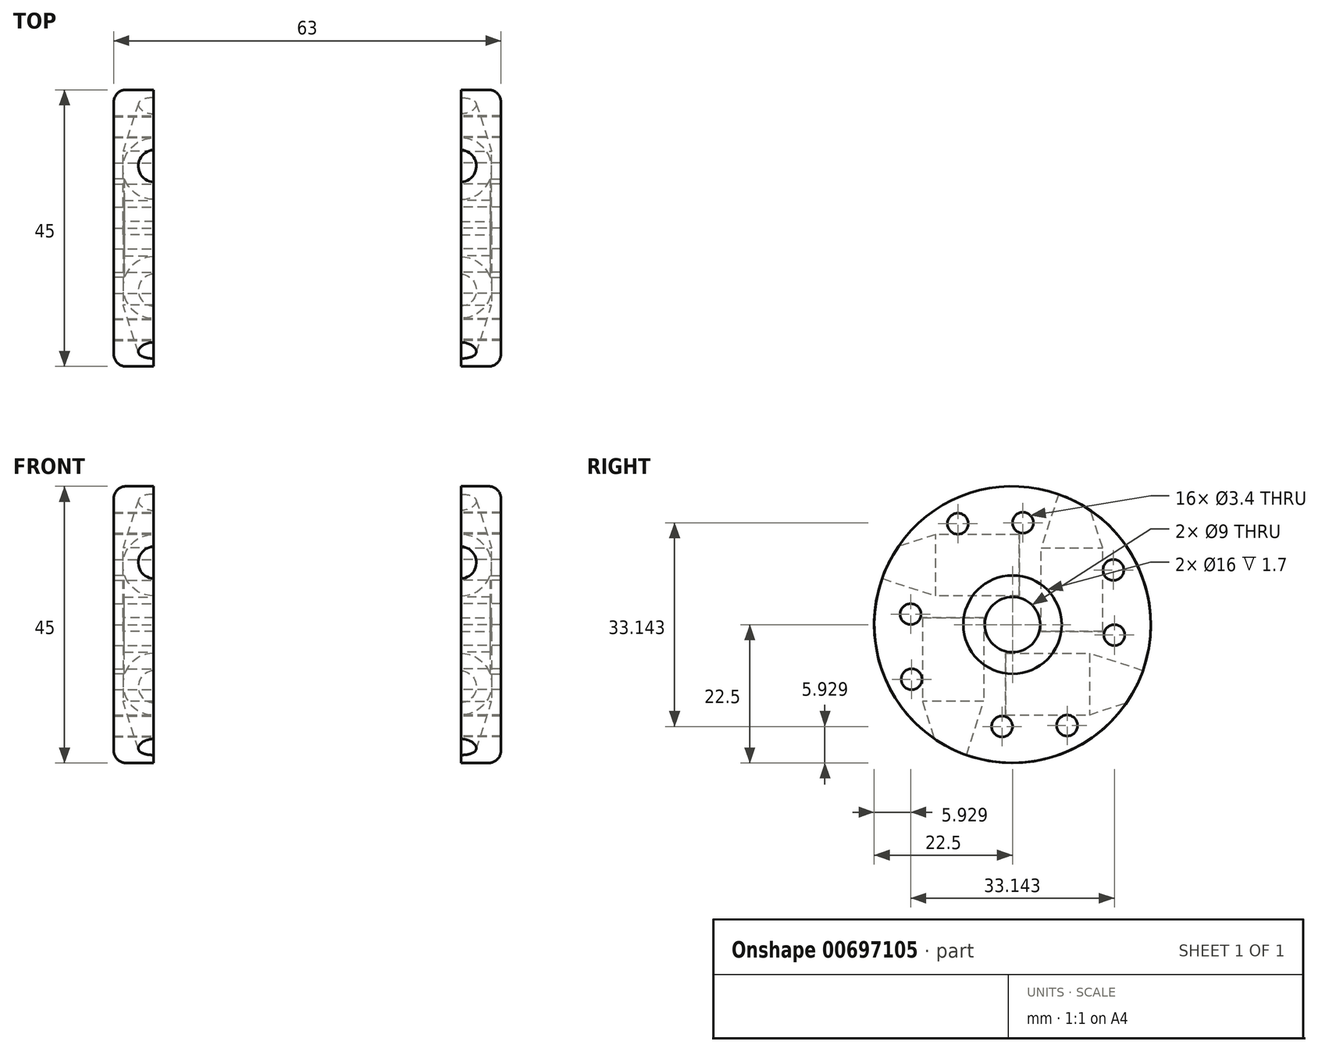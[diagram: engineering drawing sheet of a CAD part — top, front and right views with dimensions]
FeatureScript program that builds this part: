
annotation { "Feature Type Name" : "Feature", "Feature Type Description" : "" }
export const myFeature = defineFeature(function(context is Context, id is Id, definition is map)
    precondition{}
    {
        {
            var Q0;
            Q0=qCreatedBy(makeId("Right.planeOp"),FACE);
            var sketch = newSketch(context, id + "F0", { "sketchPlane" : qUnion([Q0])});
            skCircle(sketch, "E0", {"center": v(0, 0) * mm, "radius": 22.5 * mm});
            skCircle(sketch, "E1", {"center": v(0, 0) * mm, "radius": 4.5 * mm});
            skCircle(sketch, "E2", {"center": v(1.7, 16.57) * mm, "radius": 1.7 * mm});
            skCircle(sketch, "E3", {"center": v(-8.89, 16.41) * mm, "radius": 1.7 * mm});
            skCircle(sketch, "E4.1.0", {"center": v(-16.57, 1.7) * mm, "radius": 1.7 * mm});
            skCircle(sketch, "E4.1.1", {"center": v(-16.41, -8.89) * mm, "radius": 1.7 * mm});
            skCircle(sketch, "E4.2.0", {"center": v(-1.7, -16.57) * mm, "radius": 1.7 * mm});
            skCircle(sketch, "E4.2.1", {"center": v(8.89, -16.41) * mm, "radius": 1.7 * mm});
            skCircle(sketch, "E4.3.0", {"center": v(16.57, -1.7) * mm, "radius": 1.7 * mm});
            skCircle(sketch, "E4.3.1", {"center": v(16.41, 8.89) * mm, "radius": 1.7 * mm});
            skSolve(sketch);
        }
        {
            var Q0;
            Q0=makeQuery(id+"F0.imprint","IMPRINT",FACE,{"disambiguationData":[TD([[makeQuery(id+"F0.imprint","IMPRINT",EDGE,{"derivedFrom":sQuery(id+"F0.wireOp",EDGE,"E0")}),1.0]])]});
            var Q1;
            Q1=makeQuery(id+"F0.imprint","IMPRINT",FACE,{"disambiguationData":[TD([[makeQuery(id+"F0.imprint","IMPRINT",EDGE,{"derivedFrom":sQuery(id+"F0.wireOp",EDGE,"E1")}),-1.0]])]});
            extrude(context, id + "F1", {"entities" : qUnion([Q0, Q1]), "depth" : 6.5 * mm, "offsetDistance" : 25 * mm});
        }
        {
            var Q0;
            Q0=qCreatedBy(makeId("Top.planeOp"),FACE);
            var sketch = newSketch(context, id + "F2", { "sketchPlane" : qUnion([Q0])});
            skLineSegment(sketch, "E5", {"start": v(-19.71, 0) * mm, "end": v(30.41, 0) * mm});
            skSolve(sketch);
        }
        {
            var Q0;
            Q0=qCreatedBy(makeId("Right.planeOp"),FACE);
            var sketch = newSketch(context, id + "F3", { "sketchPlane" : qUnion([Q0])});
            skLineSegment(sketch, "E6.top", {"start": v(1.1, 9.67) * mm, "end": v(1.1, 4.67) * mm});
            skLineSegment(sketch, "E6.left", {"start": v(-12.5, 9.67) * mm, "end": v(1.1, 9.67) * mm});
            skLineSegment(sketch, "E6.right", {"start": v(-12.5, 4.67) * mm, "end": v(1.1, 4.67) * mm});
            skLineSegment(sketch, "E7", {"start": v(-12.5, 4.67) * mm, "end": v(-24.5, 8.57) * mm});
            skLineSegment(sketch, "E8", {"start": v(-24.5, 8.57) * mm, "end": v(-24.5, 9.67) * mm});
            skLineSegment(sketch, "E9", {"start": v(-24.5, 9.67) * mm, "end": v(-12.5, 9.67) * mm});
            skSolve(sketch);
        }
        {
            var Q0;
            Q0=makeQuery(id+"F3.imprint","IMPRINT",FACE,{"disambiguationData":[TD([[makeQuery(id+"F3.imprint","IMPRINT",EDGE,{"derivedFrom":sQuery(id+"F3.wireOp",EDGE,"E6.top")}),-1.0]])]});
            var Q1;
            Q1=sQuery(id+"F3.wireOp",EDGE,"E9");
            revolve(context, id + "F4", {"entities" : qUnion([Q0]), "axis" : qUnion([Q1]), "revolveType" : RevolveType.FULL});
        }
        {
            var Q0;
            Q0=makeQuery(id+"F4.opRevolve","SWEPT_BODY",BODY,{"disambiguationData":[OSD([sQuery(id+"F3.wireOp",EDGE,"E6.top"),sQuery(id+"F3.wireOp",EDGE,"E6.left"),sQuery(id+"F3.wireOp",EDGE,"E6.right"),sQuery(id+"F3.wireOp",EDGE,"E7"),sQuery(id+"F3.wireOp",EDGE,"E8"),sQuery(id+"F3.wireOp",EDGE,"E9")])]});
            var Q1;
            Q1=sQuery(id+"F2.wireOp",EDGE,"E5");
            circularPattern(context, id + "F5", {"entities" : qUnion([Q0]), "axis" : qUnion([Q1]), "angle" : 360 * degree, "instanceCount" : 4, "equalSpace" : true});
        }
        {
            var Q0;
            Q0=makeQuery(id+"F4.opRevolve","SWEPT_BODY",BODY,{"disambiguationData":[OSD([sQuery(id+"F3.wireOp",EDGE,"E6.top"),sQuery(id+"F3.wireOp",EDGE,"E6.left"),sQuery(id+"F3.wireOp",EDGE,"E6.right"),sQuery(id+"F3.wireOp",EDGE,"E7"),sQuery(id+"F3.wireOp",EDGE,"E8"),sQuery(id+"F3.wireOp",EDGE,"E9")])]});
            var Q1;
            Q1=makeQuery(id+"F5.opPattern","COPY",BODY,{"derivedFrom":makeQuery(id+"F4.opRevolve","SWEPT_BODY",BODY,{"disambiguationData":[OSD([sQuery(id+"F3.wireOp",EDGE,"E6.top"),sQuery(id+"F3.wireOp",EDGE,"E6.left"),sQuery(id+"F3.wireOp",EDGE,"E6.right"),sQuery(id+"F3.wireOp",EDGE,"E7"),sQuery(id+"F3.wireOp",EDGE,"E8"),sQuery(id+"F3.wireOp",EDGE,"E9")])]}),"instanceName":"3"});
            var Q2;
            Q2=makeQuery(id+"F5.opPattern","COPY",BODY,{"derivedFrom":makeQuery(id+"F4.opRevolve","SWEPT_BODY",BODY,{"disambiguationData":[OSD([sQuery(id+"F3.wireOp",EDGE,"E6.top"),sQuery(id+"F3.wireOp",EDGE,"E6.left"),sQuery(id+"F3.wireOp",EDGE,"E6.right"),sQuery(id+"F3.wireOp",EDGE,"E7"),sQuery(id+"F3.wireOp",EDGE,"E8"),sQuery(id+"F3.wireOp",EDGE,"E9")])]}),"instanceName":"2"});
            var Q3;
            Q3=makeQuery(id+"F5.opPattern","COPY",BODY,{"derivedFrom":makeQuery(id+"F4.opRevolve","SWEPT_BODY",BODY,{"disambiguationData":[OSD([sQuery(id+"F3.wireOp",EDGE,"E6.top"),sQuery(id+"F3.wireOp",EDGE,"E6.left"),sQuery(id+"F3.wireOp",EDGE,"E6.right"),sQuery(id+"F3.wireOp",EDGE,"E7"),sQuery(id+"F3.wireOp",EDGE,"E8"),sQuery(id+"F3.wireOp",EDGE,"E9")])]}),"instanceName":"1"});
            var Q4;
            Q4=makeQuery(id+"F1.opExtrude","SWEPT_BODY",BODY,{"disambiguationData":[OSD([sQuery(id+"F0.wireOp",EDGE,"E0"),sQuery(id+"F0.wireOp",EDGE,"E1"),sQuery(id+"F0.wireOp",EDGE,"E2"),sQuery(id+"F0.wireOp",EDGE,"cbc2b849-6399-4062-8aac-5185108daa26.1.0"),sQuery(id+"F0.wireOp",EDGE,"cbc2b849-6399-4062-8aac-5185108daa26.2.0"),sQuery(id+"F0.wireOp",EDGE,"cbc2b849-6399-4062-8aac-5185108daa26.3.0")])]});
            booleanBodies(context, id + "F6", {"operationType" : BooleanOperationType.SUBTRACTION, "tools" : qUnion([Q0, Q1, Q2, Q3]), "targets" : qUnion([Q4])});
        }
        {
            var Q0;
            Q0=qCreatedBy(makeId("Right.planeOp"),FACE);
            cPlane(context, id + "F7", {"entities" : qUnion([Q0]), "cplaneType" : CPlaneType.OFFSET, "offset" : 25 * mm, "oppositeDirection" : true, "width" : 150 * mm, "height" : 150 * mm});
        }
        {
            var Q0;
            Q0=makeQuery(id+"F1.opExtrude","CAP_EDGE",EDGE,{"disambiguationData":[OSD([sQuery(id+"F0.wireOp",EDGE,"E0")])],"isStart":false});
            fillet(context, id + "F8", {"entities" : qUnion([Q0]), "radius" : 2 * mm, "tangentPropagation" : true, "allowEdgeOverflow" : false});
        }
        {
            var Q0;
            Q0=makeQuery(id+"F1.opExtrude","CAP_FACE",FACE,{"disambiguationData":[OSD([sQuery(id+"F0.wireOp",EDGE,"E0"),sQuery(id+"F0.wireOp",EDGE,"E1"),sQuery(id+"F0.wireOp",EDGE,"E2"),sQuery(id+"F0.wireOp",EDGE,"E3"),sQuery(id+"F0.wireOp",EDGE,"E4.1.0"),sQuery(id+"F0.wireOp",EDGE,"E4.1.1"),sQuery(id+"F0.wireOp",EDGE,"E4.2.0"),sQuery(id+"F0.wireOp",EDGE,"E4.2.1"),sQuery(id+"F0.wireOp",EDGE,"E4.3.0"),sQuery(id+"F0.wireOp",EDGE,"E4.3.1")])],"isStart":false});
            var sketch = newSketch(context, id + "F9", { "sketchPlane" : qUnion([Q0])});
            skCircle(sketch, "E10", {"center": v(0, 0) * mm, "radius": 8 * mm});
            skSolve(sketch);
        }
        {
            var Q0;
            Q0=makeQuery(id+"F9.imprint","IMPRINT",FACE,{"disambiguationData":[TD([[makeQuery(id+"F9.imprint","IMPRINT",EDGE,{"derivedFrom":sQuery(id+"F9.wireOp",EDGE,"E10")}),1.0]])]});
            extrude(context, id + "F10", {"entities" : qUnion([Q0]), "operationType" : NewBodyOperationType.REMOVE, "oppositeDirection" : true, "depth" : 1.7 * mm, "offsetDistance" : 25 * mm});
        }
        {
            var Q0;
            Q0=makeQuery(id+"F1.opExtrude","SWEPT_BODY",BODY,{"disambiguationData":[OSD([sQuery(id+"F0.wireOp",EDGE,"E0"),sQuery(id+"F0.wireOp",EDGE,"E1"),sQuery(id+"F0.wireOp",EDGE,"E2"),sQuery(id+"F0.wireOp",EDGE,"cbc2b849-6399-4062-8aac-5185108daa26.1.0"),sQuery(id+"F0.wireOp",EDGE,"cbc2b849-6399-4062-8aac-5185108daa26.2.0"),sQuery(id+"F0.wireOp",EDGE,"cbc2b849-6399-4062-8aac-5185108daa26.3.0")])]});
            var Q1;
            Q1=qCreatedBy(id+"F7.planeOp",FACE);
            mirror(context, id + "F11", {"entities" : qUnion([Q0]), "mirrorPlane" : qUnion([Q1])});
        }
    });
